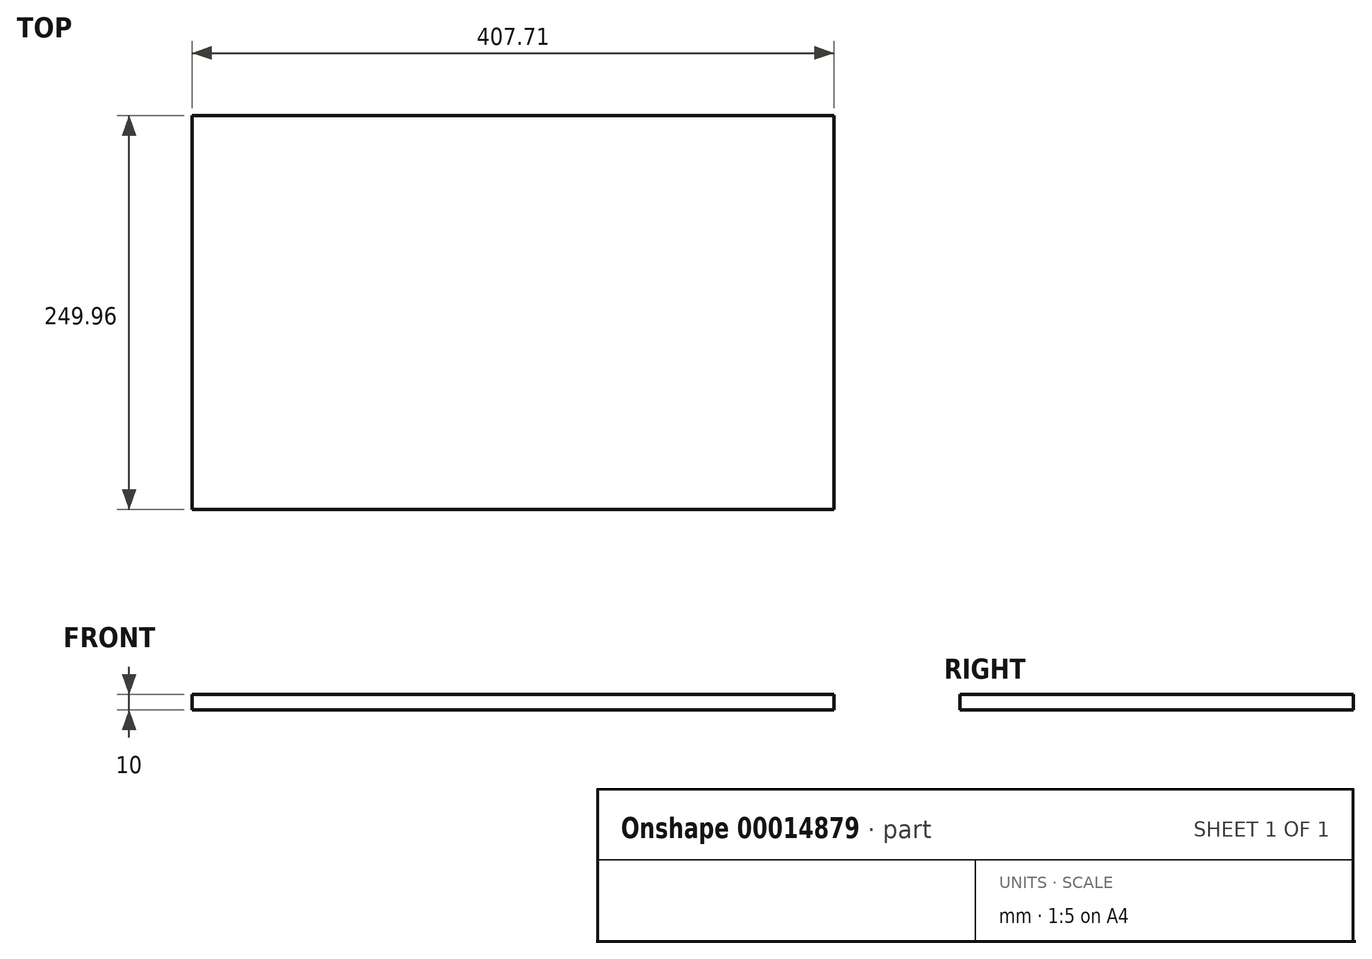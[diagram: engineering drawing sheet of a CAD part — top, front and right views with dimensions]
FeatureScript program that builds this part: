
annotation { "Feature Type Name" : "Feature", "Feature Type Description" : "" }
export const myFeature = defineFeature(function(context is Context, id is Id, definition is map)
    precondition{}
    {
        {
            var Q0;
            Q0=qCreatedBy(makeId("Top.planeOp"),FACE);
            var sketch = newSketch(context, id + "F0", { "sketchPlane" : qUnion([Q0])});
            skLineSegment(sketch, "E0.bottom", {"start": v(-109.97, 53.67) * mm, "end": v(297.74, 53.67) * mm});
            skLineSegment(sketch, "E0.top", {"start": v(-109.97, -196.29) * mm, "end": v(297.74, -196.29) * mm});
            skLineSegment(sketch, "E0.left", {"start": v(-109.97, 53.67) * mm, "end": v(-109.97, -196.29) * mm});
            skLineSegment(sketch, "E0.right", {"start": v(297.74, 53.67) * mm, "end": v(297.74, -196.29) * mm});
            skSolve(sketch);
        }
        {
            var Q0;
            Q0=makeQuery(id+"F0.imprint","IMPRINT",FACE,{"disambiguationData":[TD([[makeQuery(id+"F0.imprint","IMPRINT",EDGE,{"derivedFrom":sQuery(id+"F0.wireOp",EDGE,"E0.bottom")}),-1.0]])]});
            extrude(context, id + "F1", {"entities" : qUnion([Q0]), "oppositeDirection" : true, "depth" : 10 * mm});
        }
    });
